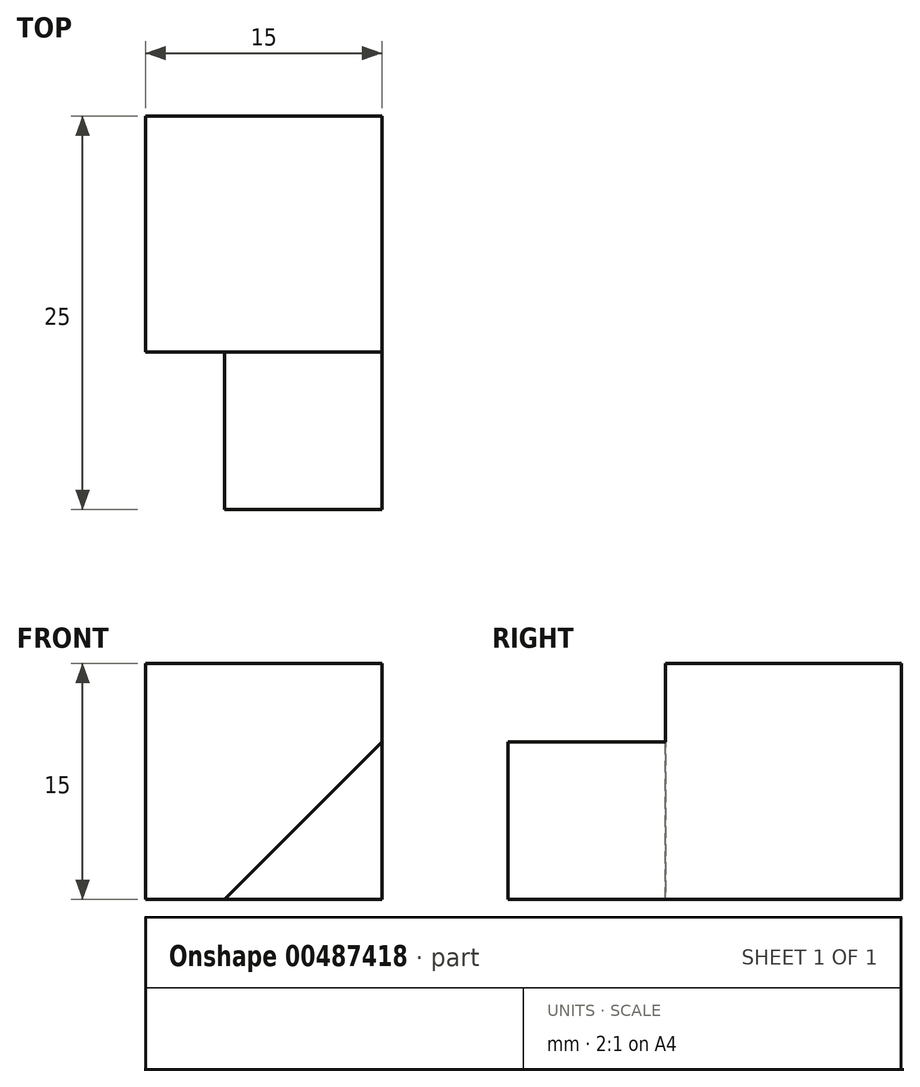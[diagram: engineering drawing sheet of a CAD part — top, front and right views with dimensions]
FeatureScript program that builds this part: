
annotation { "Feature Type Name" : "Feature", "Feature Type Description" : "" }
export const myFeature = defineFeature(function(context is Context, id is Id, definition is map)
    precondition{}
    {
        {
            var Q0;
            Q0=qCreatedBy(makeId("Top.planeOp"),FACE);
            var sketch = newSketch(context, id + "F0", { "sketchPlane" : qUnion([Q0])});
            skLineSegment(sketch, "E0.bottom", {"start": v(-2.18, 10.47) * mm, "end": v(12.82, 10.47) * mm});
            skLineSegment(sketch, "E0.top", {"start": v(-2.18, -4.53) * mm, "end": v(12.82, -4.53) * mm});
            skLineSegment(sketch, "E0.left", {"start": v(-2.18, 10.47) * mm, "end": v(-2.18, -4.53) * mm});
            skLineSegment(sketch, "E0.right", {"start": v(12.82, 10.47) * mm, "end": v(12.82, -4.53) * mm});
            skSolve(sketch);
        }
        {
            var Q0;
            Q0=makeQuery(id+"F0.imprint","IMPRINT",FACE,{"disambiguationData":[TD([[makeQuery(id+"F0.imprint","IMPRINT",EDGE,{"derivedFrom":sQuery(id+"F0.wireOp",EDGE,"E0.bottom")}),-1.0]])]});
            extrude(context, id + "F1", {"entities" : qUnion([Q0]), "depth" : 15 * mm});
        }
        {
            var Q0;
            Q0=makeQuery(id+"F1.opExtrude","SWEPT_FACE",FACE,{"disambiguationData":[OSD([sQuery(id+"F0.wireOp",EDGE,"E0.top")])]});
            var sketch = newSketch(context, id + "F2", { "sketchPlane" : qUnion([Q0])});
            skLineSegment(sketch, "E1", {"start": v(12.82, 10) * mm, "end": v(12.82, 0) * mm});
            skLineSegment(sketch, "E2", {"start": v(12.82, 0) * mm, "end": v(2.82, 0) * mm});
            skLineSegment(sketch, "E3", {"start": v(2.82, 0) * mm, "end": v(12.82, 10) * mm});
            skSolve(sketch);
        }
        {
            var Q0;
            Q0=makeQuery(id+"F2.imprint","IMPRINT",FACE,{"disambiguationData":[TD([[makeQuery(id+"F2.imprint","IMPRINT",EDGE,{"derivedFrom":sQuery(id+"F2.wireOp",EDGE,"E1")}),-1.0]])]});
            extrude(context, id + "F3", {"entities" : qUnion([Q0]), "operationType" : NewBodyOperationType.ADD, "depth" : 10 * mm});
        }
    });
